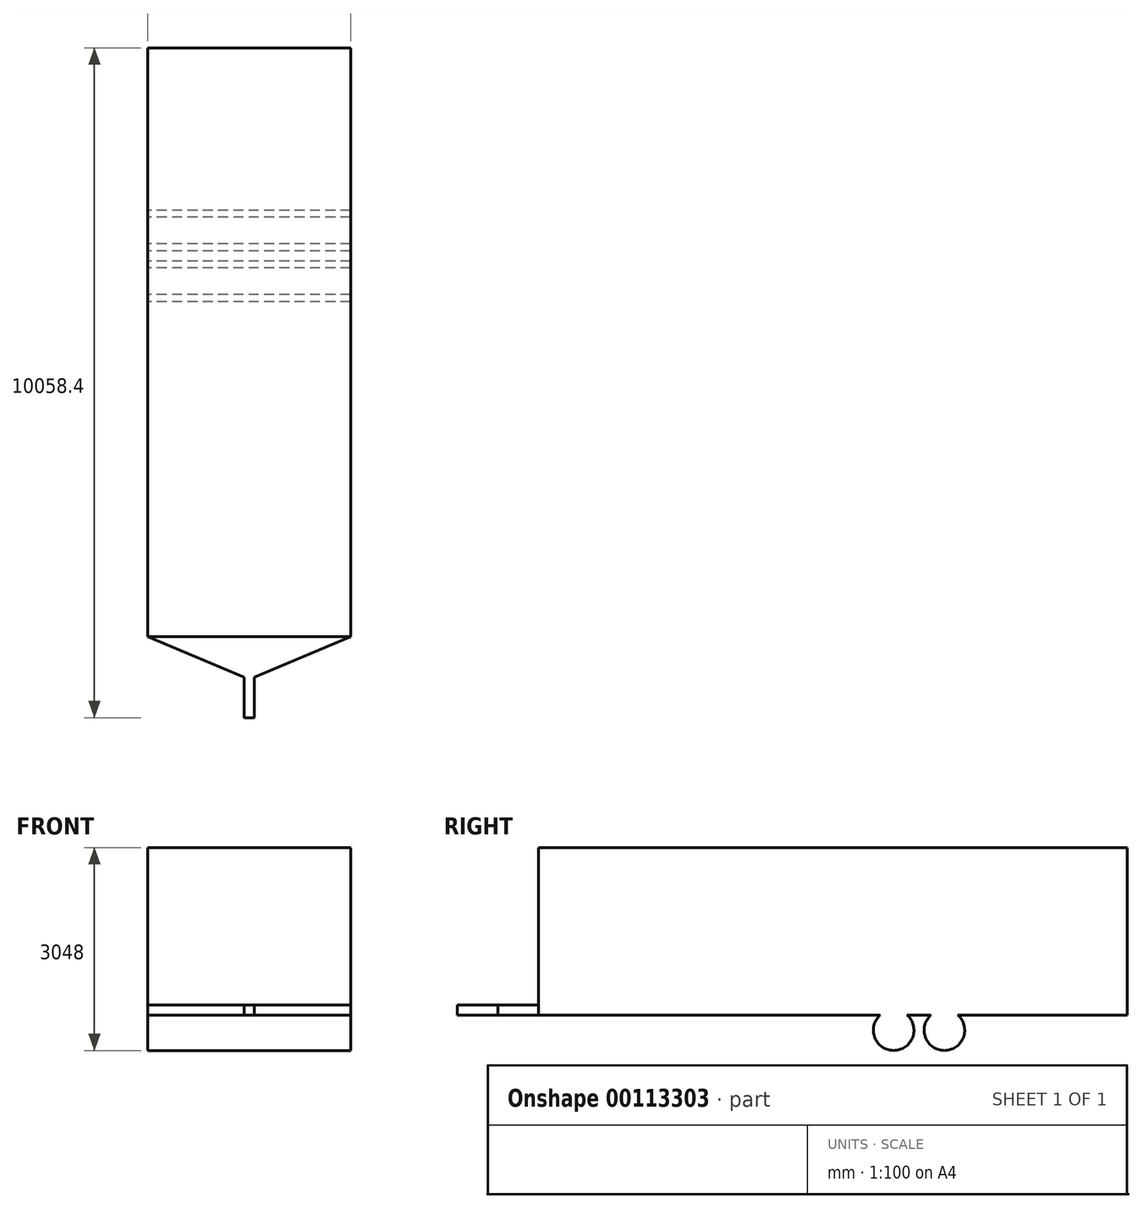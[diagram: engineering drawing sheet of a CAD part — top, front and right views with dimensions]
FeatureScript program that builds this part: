
annotation { "Feature Type Name" : "Feature", "Feature Type Description" : "" }
export const myFeature = defineFeature(function(context is Context, id is Id, definition is map)
    precondition{}
    {
        {
            var Q0;
            Q0=qCreatedBy(makeId("Top.planeOp"),FACE);
            var sketch = newSketch(context, id + "F0", { "sketchPlane" : qUnion([Q0])});
            skLineSegment(sketch, "E0.bottom", {"start": v(76.2, -304.8) * mm, "end": v(-76.2, -304.8) * mm});
            skLineSegment(sketch, "E0.top", {"start": v(76.2, 304.8) * mm, "end": v(-76.2, 304.8) * mm});
            skLineSegment(sketch, "E0.left", {"start": v(76.2, -304.8) * mm, "end": v(76.2, 304.8) * mm});
            skLineSegment(sketch, "E0.right", {"start": v(-76.2, -304.8) * mm, "end": v(-76.2, 304.8) * mm});
            skPoint(sketch, "E0.middle", {"position": v(0, 0) * mm});
            skLineSegment(sketch, "E1", {"start": v(-76.2, 304.8) * mm, "end": v(-1524, 914.4) * mm});
            skLineSegment(sketch, "E2", {"start": v(-1524, 914.4) * mm, "end": v(1524, 914.4) * mm});
            skLineSegment(sketch, "E3", {"start": v(1524, 914.4) * mm, "end": v(76.2, 304.8) * mm});
            skLineSegment(sketch, "E4", {"start": v(0, 304.8) * mm, "end": v(0, 914.4) * mm, "construction": true});
            skLineSegment(sketch, "E5.top", {"start": v(-1524, 9753.6) * mm, "end": v(1524, 9753.6) * mm});
            skLineSegment(sketch, "E5.left", {"start": v(-1524, 914.4) * mm, "end": v(-1524, 9753.6) * mm});
            skLineSegment(sketch, "E5.right", {"start": v(1524, 914.4) * mm, "end": v(1524, 9753.6) * mm});
            skSolve(sketch);
        }
        {
            var Q0;
            Q0 = qSketchRegion(id + "F0", true);
            extrude(context, id + "F1", {"entities" : qUnion([Q0]), "depth" : 3048 * mm});
        }
        {
            var Q0;
            Q0=makeQuery(id+"F1.opExtrude","SWEPT_FACE",FACE,{"disambiguationData":[OSD([sQuery(id+"F0.wireOp",EDGE,"E5.left")])]});
            var sketch = newSketch(context, id + "F2", { "sketchPlane" : qUnion([Q0])});
            skLineSegment(sketch, "E6", {"start": v(-9753.6, 533.4) * mm, "end": v(-7212, 533.4) * mm});
            skLineSegment(sketch, "E7", {"start": v(304.8, 533.4) * mm, "end": v(-6046.8, 533.4) * mm});
            skArc(sketch, "E8", {"start": v(-7212, 533.4) * mm, "mid": v(-7010.4, 0) * mm, "end": v(-6808.8, 533.4) * mm});
            skArc(sketch, "E9", {"start": v(-6450, 533.4) * mm, "mid": v(-6248.4, 0) * mm, "end": v(-6046.8, 533.4) * mm});
            skLineSegment(sketch, "E10", {"start": v(-6808.8, 533.4) * mm, "end": v(-6450, 533.4) * mm});
            skLineSegment(sketch, "E11", {"start": v(-9753.6, 533.4) * mm, "end": v(-9753.6, 0) * mm});
            skLineSegment(sketch, "E12", {"start": v(-9753.6, 0) * mm, "end": v(304.8, 0) * mm});
            skLineSegment(sketch, "E13", {"start": v(304.8, 0) * mm, "end": v(304.8, 533.4) * mm});
            skLineSegment(sketch, "E14", {"start": v(-914.4, 3048) * mm, "end": v(-914.4, 685.8) * mm});
            skLineSegment(sketch, "E15", {"start": v(-914.4, 685.8) * mm, "end": v(304.8, 685.8) * mm});
            skLineSegment(sketch, "E16", {"start": v(304.8, 685.8) * mm, "end": v(304.8, 3048) * mm});
            skLineSegment(sketch, "E17", {"start": v(304.8, 3048) * mm, "end": v(-914.4, 3048) * mm});
            skSolve(sketch);
        }
        {
            var Q0;
            Q0 = qSketchRegion(id + "F2", true);
            extrude(context, id + "F3", {"entities" : qUnion([Q0]), "operationType" : NewBodyOperationType.REMOVE, "endBound" : BoundingType.THROUGH_ALL, "oppositeDirection" : true, "depth" : 1369.86 * mm});
        }
    });
